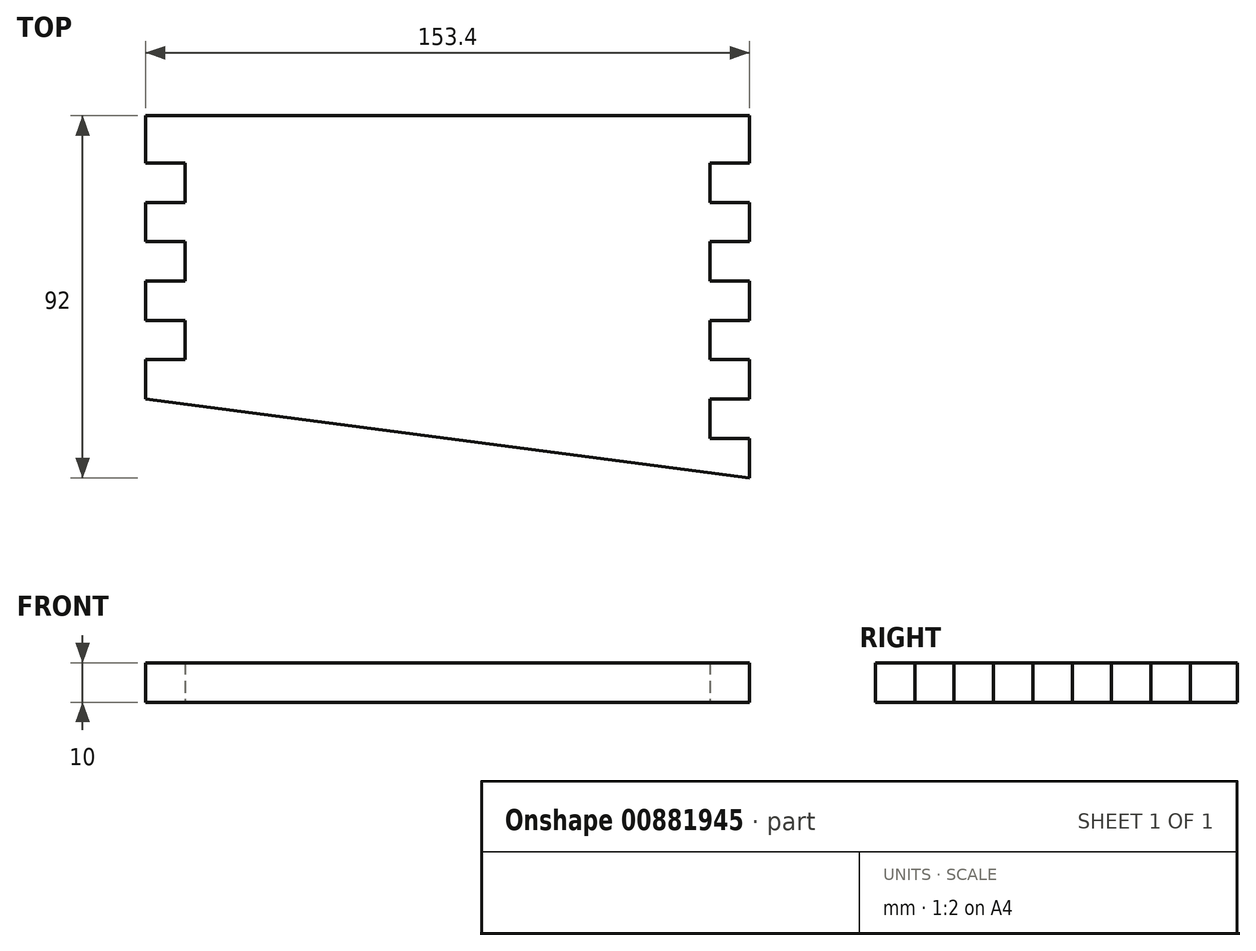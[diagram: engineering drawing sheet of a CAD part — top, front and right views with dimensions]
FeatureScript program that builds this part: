
annotation { "Feature Type Name" : "Feature", "Feature Type Description" : "" }
export const myFeature = defineFeature(function(context is Context, id is Id, definition is map)
    precondition{}
    {
        {
            var Q0;
            Q0=qCreatedBy(makeId("Top.planeOp"),FACE);
            var sketch = newSketch(context, id + "F0", { "sketchPlane" : qUnion([Q0])});
            skLineSegment(sketch, "E0.bottom", {"start": v(-145.63, 36.94) * mm, "end": v(7.77, 36.94) * mm});
            skLineSegment(sketch, "E0.top", {"start": v(-145.63, -33.06) * mm, "end": v(7.77, -33.06) * mm});
            skLineSegment(sketch, "E0.left", {"start": v(-145.63, 36.94) * mm, "end": v(-145.63, -33.06) * mm});
            skLineSegment(sketch, "E0.right", {"start": v(7.77, 36.94) * mm, "end": v(7.77, -33.06) * mm});
            skLineSegment(sketch, "E1.bottom", {"start": v(-145.63, 36.94) * mm, "end": v(-135.63, 36.94) * mm});
            skLineSegment(sketch, "E1.top", {"start": v(-145.63, -33.06) * mm, "end": v(-135.63, -33.06) * mm});
            skLineSegment(sketch, "E1.right", {"start": v(-135.63, 36.94) * mm, "end": v(-135.63, -33.06) * mm});
            skLineSegment(sketch, "E2.bottom", {"start": v(7.77, 36.94) * mm, "end": v(-2.23, 36.94) * mm});
            skLineSegment(sketch, "E2.top", {"start": v(7.77, -33.06) * mm, "end": v(-2.23, -33.06) * mm});
            skLineSegment(sketch, "E2.right", {"start": v(-2.23, 36.94) * mm, "end": v(-2.23, -33.06) * mm});
            skLineSegment(sketch, "E3.left", {"start": v(-145.63, 36.94) * mm, "end": v(-145.63, 26.94) * mm});
            skLineSegment(sketch, "E4.bottom", {"start": v(-2.23, 36.94) * mm, "end": v(7.77, 36.94) * mm});
            skLineSegment(sketch, "E4.top", {"start": v(-2.23, 26.94) * mm, "end": v(7.77, 26.94) * mm});
            skLineSegment(sketch, "E4.left", {"start": v(-2.23, 36.94) * mm, "end": v(-2.23, 26.94) * mm});
            skLineSegment(sketch, "E4.right", {"start": v(7.77, 36.94) * mm, "end": v(7.77, 26.94) * mm});
            skLineSegment(sketch, "E5.MirrorCS", {"start": v(7.77, 16.94) * mm, "end": v(-2.23, 16.94) * mm});
            skLineSegment(sketch, "E6.MirrorCS", {"start": v(-2.23, 6.94) * mm, "end": v(7.77, 6.94) * mm});
            skLineSegment(sketch, "E7.MirrorCS", {"start": v(7.77, -3.06) * mm, "end": v(-2.23, -3.06) * mm});
            skLineSegment(sketch, "E8.MirrorCS", {"start": v(-2.23, -13.06) * mm, "end": v(7.77, -13.06) * mm});
            skLineSegment(sketch, "E9.MirrorCS", {"start": v(7.77, -23.06) * mm, "end": v(-2.23, -23.06) * mm});
            skLineSegment(sketch, "E10.MirrorCS", {"start": v(-2.23, -33.06) * mm, "end": v(7.77, -33.06) * mm});
            skLineSegment(sketch, "E11.top", {"start": v(-145.63, 26.94) * mm, "end": v(-135.63, 26.94) * mm});
            skLineSegment(sketch, "E11.right", {"start": v(-135.63, 36.94) * mm, "end": v(-135.63, 26.94) * mm});
            skLineSegment(sketch, "E12.MirrorCS", {"start": v(-145.63, 16.94) * mm, "end": v(-135.63, 16.94) * mm});
            skLineSegment(sketch, "E13.MirrorCS", {"start": v(-145.63, 6.94) * mm, "end": v(-135.63, 6.94) * mm});
            skLineSegment(sketch, "E14.MirrorCS", {"start": v(-145.63, -3.06) * mm, "end": v(-135.63, -3.06) * mm});
            skLineSegment(sketch, "E15.MirrorCS", {"start": v(-145.63, -13.06) * mm, "end": v(-135.63, -13.06) * mm});
            skLineSegment(sketch, "E16.MirrorCS", {"start": v(-145.63, -23.06) * mm, "end": v(-135.63, -23.06) * mm});
            skLineSegment(sketch, "E17", {"start": v(7.77, -33.06) * mm, "end": v(7.77, -53.06) * mm});
            skLineSegment(sketch, "E18", {"start": v(7.77, -53.06) * mm, "end": v(-145.63, -33.06) * mm});
            skLineSegment(sketch, "E19", {"start": v(-2.23, -33.06) * mm, "end": v(-2.23, -51.75) * mm});
            skLineSegment(sketch, "E20.MirrorCS", {"start": v(7.77, -43.06) * mm, "end": v(-2.23, -43.06) * mm});
            skLineSegment(sketch, "E21.top", {"start": v(-145.63, 38.94) * mm, "end": v(7.77, 38.94) * mm});
            skLineSegment(sketch, "E21.left", {"start": v(-145.63, 36.94) * mm, "end": v(-145.63, 38.94) * mm});
            skLineSegment(sketch, "E21.right", {"start": v(7.77, 36.94) * mm, "end": v(7.77, 38.94) * mm});
            skLineSegment(sketch, "E22", {"start": v(-135.63, 36.94) * mm, "end": v(-135.63, -34.36) * mm, "construction": true});
            skSolve(sketch);
        }
        {
            var Q0;
            {var subQ0=sQuery(id+"F0.wireOp",EDGE,"E1.right");var subQ1=sQuery(id+"F0.wireOp",EDGE,"E0.bottom");var subQ2=makeQuery(id+"F0.imprint","INTERSECT",VERTEX,{"derivedFrom":[subQ1,subQ0]});Q0=makeQuery(id+"F0.imprint","IMPRINT",FACE,{"disambiguationData":[TD([[makeQuery(id+"F0.imprint","IMPRINT",EDGE,{"disambiguationData":[TD([[subQ2,-1.0]])],"derivedFrom":subQ1}),-1.0]])]});}
            var Q1;
            {var subQ5=sQuery(id+"F0.wireOp",EDGE,"E11.top");Q1=makeQuery(id+"F0.imprint","IMPRINT",FACE,{"disambiguationData":[TD([[makeQuery(id+"F0.imprint","IMPRINT",EDGE,{"derivedFrom":subQ5}),1.0]])]});}
            var Q2;
            {var subQ0=sQuery(id+"F0.wireOp",EDGE,"E12.MirrorCS");Q2=makeQuery(id+"F0.imprint","IMPRINT",FACE,{"disambiguationData":[TD([[makeQuery(id+"F0.imprint","IMPRINT",EDGE,{"derivedFrom":subQ0}),-1.0]])]});}
            var Q3;
            {var subQ0=sQuery(id+"F0.wireOp",EDGE,"E14.MirrorCS");Q3=makeQuery(id+"F0.imprint","IMPRINT",FACE,{"disambiguationData":[TD([[makeQuery(id+"F0.imprint","IMPRINT",EDGE,{"derivedFrom":subQ0}),-1.0]])]});}
            var Q4;
            {var subQ2=sQuery(id+"F0.wireOp",EDGE,"E16.MirrorCS");Q4=makeQuery(id+"F0.imprint","IMPRINT",FACE,{"disambiguationData":[TD([[makeQuery(id+"F0.imprint","IMPRINT",EDGE,{"derivedFrom":subQ2}),-1.0]])]});}
            var Q5;
            {var subQ5=sQuery(id+"F0.wireOp",EDGE,"f68d17bd-8033-4fb8-93ba-191072b4510d0.MirrorCS");Q5=makeQuery(id+"F0.imprint","IMPRINT",FACE,{"disambiguationData":[TD([[makeQuery(id+"F0.imprint","IMPRINT",EDGE,{"derivedFrom":subQ5}),-1.0]])]});}
            var Q6;
            {var subQ5=sQuery(id+"F0.wireOp",EDGE,"e518cc57-b2af-43e8-af13-6bb7c84993f30.MirrorCS");Q6=makeQuery(id+"F0.imprint","IMPRINT",FACE,{"disambiguationData":[TD([[makeQuery(id+"F0.imprint","IMPRINT",EDGE,{"derivedFrom":subQ5}),1.0]])]});}
            var Q7;
            {var subQ5=sQuery(id+"F0.wireOp",EDGE,"E4.top");Q7=makeQuery(id+"F0.imprint","IMPRINT",FACE,{"disambiguationData":[TD([[makeQuery(id+"F0.imprint","IMPRINT",EDGE,{"derivedFrom":subQ5}),1.0]])]});}
            var Q8;
            {var subQ0=sQuery(id+"F0.wireOp",EDGE,"E5.MirrorCS");Q8=makeQuery(id+"F0.imprint","IMPRINT",FACE,{"disambiguationData":[TD([[makeQuery(id+"F0.imprint","IMPRINT",EDGE,{"derivedFrom":subQ0}),1.0]])]});}
            var Q9;
            {var subQ0=sQuery(id+"F0.wireOp",EDGE,"E7.MirrorCS");Q9=makeQuery(id+"F0.imprint","IMPRINT",FACE,{"disambiguationData":[TD([[makeQuery(id+"F0.imprint","IMPRINT",EDGE,{"derivedFrom":subQ0}),1.0]])]});}
            var Q10;
            {var subQ0=sQuery(id+"F0.wireOp",EDGE,"E9.MirrorCS");Q10=makeQuery(id+"F0.imprint","IMPRINT",FACE,{"disambiguationData":[TD([[makeQuery(id+"F0.imprint","IMPRINT",EDGE,{"derivedFrom":subQ0}),1.0]])]});}
            var Q11;
            {var subQ0=sQuery(id+"F0.wireOp",EDGE,"E19");var subQ5=sQuery(id+"F0.wireOp",EDGE,"E18");var subQ7=makeQuery(id+"F0.imprint","INTERSECT",VERTEX,{"derivedFrom":[subQ5,subQ0]});Q11=makeQuery(id+"F0.imprint","IMPRINT",FACE,{"disambiguationData":[TD([[makeQuery(id+"F0.imprint","IMPRINT",EDGE,{"disambiguationData":[TD([[subQ7,1.0]])],"derivedFrom":subQ0}),-1.0]])]});}
            var Q12;
            {var subQ3=sQuery(id+"F0.wireOp",EDGE,"E20.MirrorCS");Q12=makeQuery(id+"F0.imprint","IMPRINT",FACE,{"disambiguationData":[TD([[makeQuery(id+"F0.imprint","IMPRINT",EDGE,{"derivedFrom":subQ3}),1.0]])]});}
            var Q13;
            Q13=makeQuery(id+"F0.imprint","IMPRINT",FACE,{"disambiguationData":[TD([[makeQuery(id+"F0.imprint","IMPRINT",EDGE,{"derivedFrom":sQuery(id+"F0.wireOp",EDGE,"E21.top")}),-1.0]])]});
            extrude(context, id + "F1", {"entities" : qUnion([Q0, Q1, Q2, Q3, Q4, Q5, Q6, Q7, Q8, Q9, Q10, Q11, Q12, Q13]), "depth" : 10 * mm, "offsetDistance" : 25 * mm});
        }
    });
